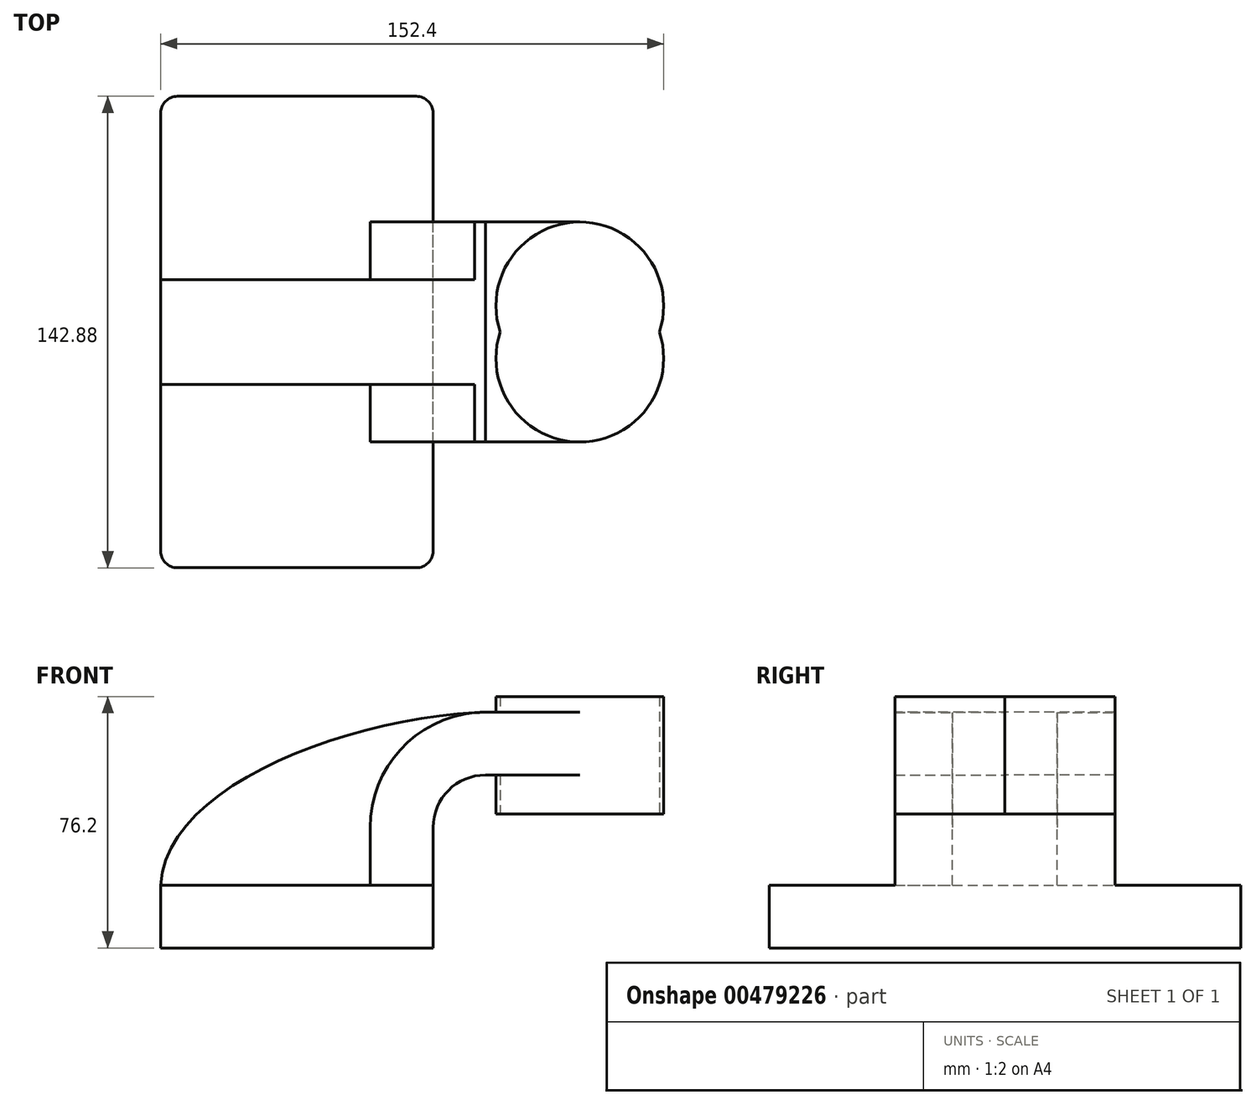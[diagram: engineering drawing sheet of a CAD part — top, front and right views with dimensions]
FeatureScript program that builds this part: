
annotation { "Feature Type Name" : "Feature", "Feature Type Description" : "" }
export const myFeature = defineFeature(function(context is Context, id is Id, definition is map)
    precondition{}
    {
        {
            var Q0;
            Q0=qCreatedBy(makeId("Front.planeOp"),FACE);
            var sketch = newSketch(context, id + "F0", { "sketchPlane" : qUnion([Q0])});
            skLineSegment(sketch, "E0.rect.bottom", {"start": v(-41.28, 9.52) * mm, "end": v(41.28, 9.52) * mm});
            skLineSegment(sketch, "E0.rect.top", {"start": v(-41.28, -9.52) * mm, "end": v(41.28, -9.52) * mm});
            skLineSegment(sketch, "E0.rect.left", {"start": v(-41.28, 9.52) * mm, "end": v(-41.28, -9.52) * mm});
            skLineSegment(sketch, "E0.rect.right", {"start": v(41.28, 9.52) * mm, "end": v(41.28, -9.52) * mm});
            skPoint(sketch, "E0.rect.middle", {"position": v(0, 0) * mm});
            skLineSegment(sketch, "E1", {"start": v(41.28, 9.52) * mm, "end": v(41.28, 27) * mm});
            skArc(sketch, "E2", {"start": v(41.28, 27) * mm, "mid": v(45.92, 38.23) * mm, "end": v(57.15, 42.88) * mm});
            skLineSegment(sketch, "E3", {"start": v(57.15, 42.88) * mm, "end": v(85.72, 42.88) * mm});
            skLineSegment(sketch, "E4.rect.bottom", {"start": v(60.32, 31.12) * mm, "end": v(111.12, 31.12) * mm});
            skLineSegment(sketch, "E4.rect.top", {"start": v(60.32, 66.68) * mm, "end": v(111.12, 66.68) * mm});
            skLineSegment(sketch, "E4.rect.left", {"start": v(60.32, 31.12) * mm, "end": v(60.32, 66.68) * mm});
            skLineSegment(sketch, "E4.rect.right", {"start": v(111.13, 31.12) * mm, "end": v(111.12, 66.68) * mm});
            skPoint(sketch, "E4.rect.middle", {"position": v(85.72, 48.9) * mm});
            skLineSegment(sketch, "E5.0", {"start": v(57.15, 61.93) * mm, "end": v(85.72, 61.93) * mm});
            skArc(sketch, "E5.1", {"start": v(22.23, 27) * mm, "mid": v(32.45, 51.7) * mm, "end": v(57.15, 61.93) * mm});
            skLineSegment(sketch, "E5.2", {"start": v(22.23, 9.52) * mm, "end": v(22.23, 27) * mm});
            skLineSegment(sketch, "E6", {"start": v(85.72, 31.12) * mm, "end": v(85.72, 66.68) * mm});
            skFitSpline(sketch, "E7", {"points": [v(-41.28, 9.53) * mm, v(57.15, 61.93) * mm], "startDerivative": vector(5.2, 92.34) * mm, "endDerivative": vector(120.92, 4.22) * mm});
            skSolve(sketch);
        }
        {
            var Q0;
            Q0=makeQuery(id+"F0.imprint","IMPRINT",FACE,{"disambiguationData":[TD([[makeQuery(id+"F0.imprint","IMPRINT",EDGE,{"derivedFrom":sQuery(id+"F0.wireOp",EDGE,"E0.rect.top")}),1.0]])]});
            extrude(context, id + "F1", {"entities" : qUnion([Q0]), "endBound" : BoundingType.SYMMETRIC, "depth" : 127 * mm});
        }
        {
            var Q0;
            {var subQ9=sQuery(id+"F0.wireOp",EDGE,"E1");Q0=makeQuery(id+"F0.imprint","IMPRINT",FACE,{"disambiguationData":[TD([[makeQuery(id+"F0.imprint","IMPRINT",EDGE,{"derivedFrom":subQ9}),1.0]])]});}
            var Q1;
            {var subQ0=sQuery(id+"F0.wireOp",EDGE,"E6");var subQ1=sQuery(id+"F0.wireOp",EDGE,"E3");var subQ2=makeQuery(id+"F0.imprint","INTERSECT",VERTEX,{"derivedFrom":[subQ1,subQ0]});Q1=makeQuery(id+"F0.imprint","IMPRINT",FACE,{"disambiguationData":[TD([[makeQuery(id+"F0.imprint","IMPRINT",EDGE,{"disambiguationData":[TD([[subQ2,1.0]])],"derivedFrom":subQ1}),1.0]])]});}
            extrude(context, id + "F2", {"entities" : qUnion([Q0, Q1]), "operationType" : NewBodyOperationType.ADD, "endBound" : BoundingType.SYMMETRIC, "depth" : 50.8 * mm});
        }
        {
            var Q0;
            {var subQ3=sQuery(id+"F0.wireOp",EDGE,"E5.2");Q0=makeQuery(id+"F0.imprint","IMPRINT",FACE,{"disambiguationData":[TD([[makeQuery(id+"F0.imprint","IMPRINT",EDGE,{"derivedFrom":subQ3}),1.0]])]});}
            extrude(context, id + "F3", {"entities" : qUnion([Q0]), "operationType" : NewBodyOperationType.ADD, "endBound" : BoundingType.SYMMETRIC, "depth" : 15.88 * mm});
        }
        {
            var Q0;
            {var subQ5=sQuery(id+"F0.wireOp",EDGE,"E4.rect.right");Q0=makeQuery(id+"F0.imprint","IMPRINT",FACE,{"disambiguationData":[TD([[makeQuery(id+"F0.imprint","IMPRINT",EDGE,{"derivedFrom":subQ5}),1.0]])]});}
            var Q1;
            Q1=sQuery(id+"F0.wireOp",EDGE,"E6");
            revolve(context, id + "F4", {"operationType" : NewBodyOperationType.ADD, "entities" : qUnion([Q0]), "axis" : qUnion([Q1]), "revolveType" : RevolveType.FULL});
        }
        {
            var Q0;
            Q0=makeQuery(id+"F1.opExtrude","CAP_EDGE",EDGE,{"disambiguationData":[OSD([sQuery(id+"F0.wireOp",EDGE,"E0.rect.right")])],"isStart":false});
            var Q1;
            Q1=makeQuery(id+"F1.opExtrude","CAP_EDGE",EDGE,{"disambiguationData":[OSD([sQuery(id+"F0.wireOp",EDGE,"E0.rect.left")])],"isStart":false});
            var Q2;
            Q2=makeQuery(id+"F1.opExtrude","CAP_EDGE",EDGE,{"disambiguationData":[OSD([sQuery(id+"F0.wireOp",EDGE,"E0.rect.right")])],"isStart":true});
            var Q3;
            Q3=makeQuery(id+"F1.opExtrude","CAP_EDGE",EDGE,{"disambiguationData":[OSD([sQuery(id+"F0.wireOp",EDGE,"E0.rect.left")])],"isStart":true});
            fillet(context, id + "F5", {"entities" : qUnion([Q0, Q1, Q2, Q3]), "radius" : 5.08 * mm, "tangentPropagation" : true, "allowEdgeOverflow" : false});
        }
        {
            var Q0;
            Q0=makeQuery(id+"F1.opExtrude","SWEPT_BODY",BODY,{"disambiguationData":[OSD([sQuery(id+"F0.wireOp",EDGE,"E0.rect.bottom"),sQuery(id+"F0.wireOp",EDGE,"E0.rect.top"),sQuery(id+"F0.wireOp",EDGE,"E0.rect.left"),sQuery(id+"F0.wireOp",EDGE,"E0.rect.right")])]});
            var Q1;
            Q1=makeQuery(id+"F3.opExtrude","CAP_FACE",FACE,{"disambiguationData":[OSD([sQuery(id+"F0.wireOp",EDGE,"E0.rect.bottom"),sQuery(id+"F0.wireOp",EDGE,"E5.1"),sQuery(id+"F0.wireOp",EDGE,"E5.2"),sQuery(id+"F0.wireOp",EDGE,"E7")])],"isStart":false});
            mirror(context, id + "F6", {"operationType" : NewBodyOperationType.ADD, "entities" : qUnion([Q0]), "mirrorPlane" : qUnion([Q1])});
        }
    });
